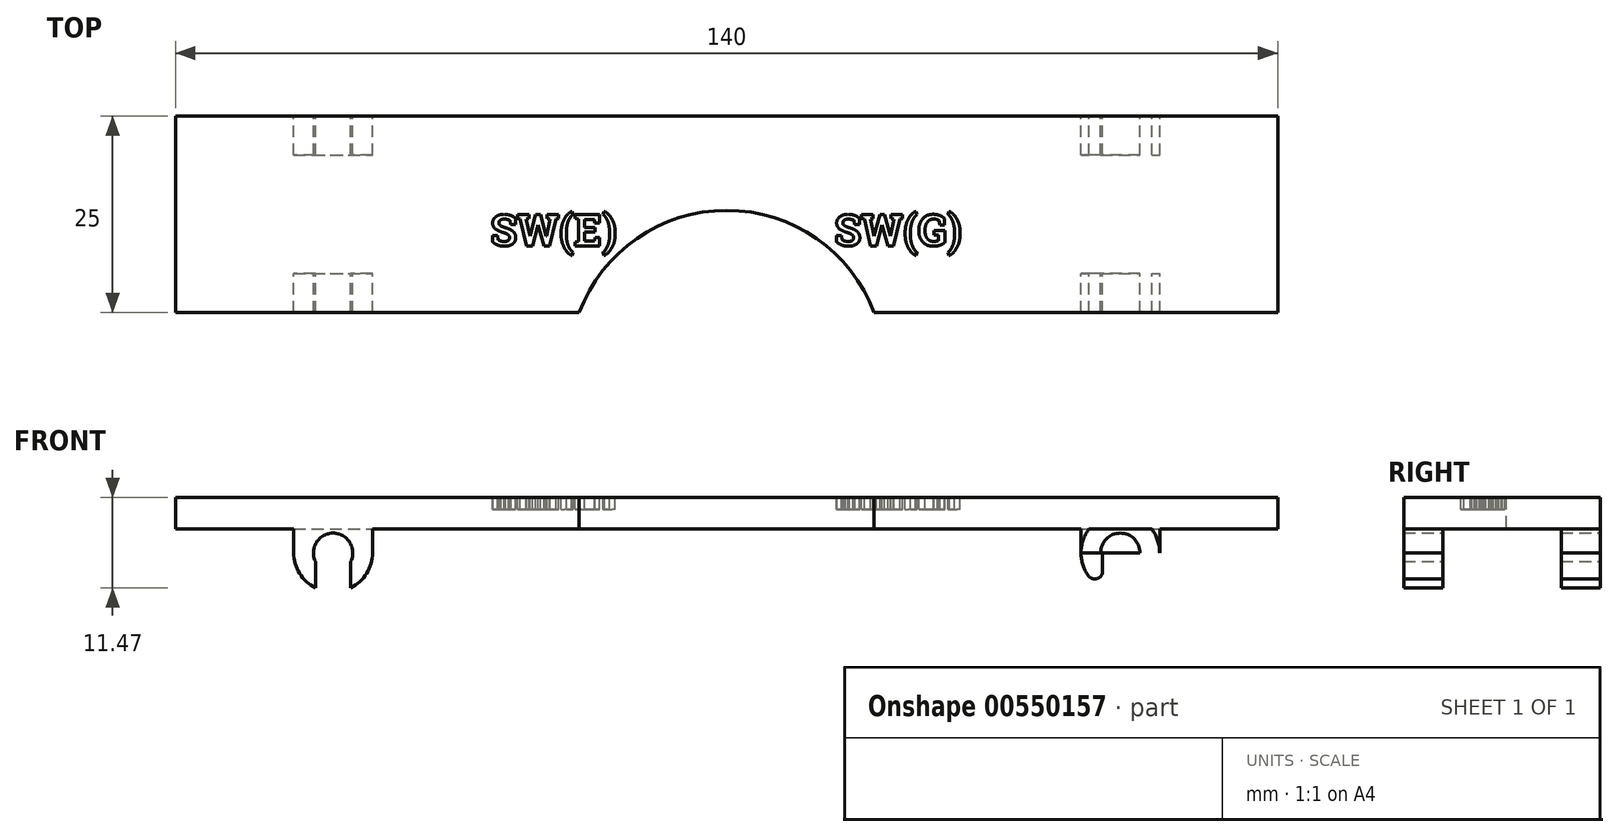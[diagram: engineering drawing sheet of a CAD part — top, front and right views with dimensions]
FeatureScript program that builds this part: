
annotation { "Feature Type Name" : "Feature", "Feature Type Description" : "" }
export const myFeature = defineFeature(function(context is Context, id is Id, definition is map)
    precondition{}
    {
        {
            var Q0;
            Q0=qCreatedBy(makeId("Top.planeOp"),FACE);
            var sketch = newSketch(context, id + "F0", { "sketchPlane" : qUnion([Q0])});
            skLineSegment(sketch, "E0.bottom", {"start": v(-70, 12.5) * mm, "end": v(70, 12.5) * mm});
            skLineSegment(sketch, "E0.top", {"start": v(-70, -12.5) * mm, "end": v(70, -12.5) * mm});
            skLineSegment(sketch, "E0.left", {"start": v(-70, 12.5) * mm, "end": v(-70, -12.5) * mm});
            skLineSegment(sketch, "E0.right", {"start": v(70, 12.5) * mm, "end": v(70, -12.5) * mm});
            skCircle(sketch, "E1", {"center": v(0, -19.5) * mm, "radius": 20 * mm});
            skSolve(sketch);
        }
        {
            var Q0;
            Q0=makeQuery(id+"F0.imprint","IMPRINT",FACE,{"disambiguationData":[TD([[makeQuery(id+"F0.imprint","IMPRINT",EDGE,{"derivedFrom":sQuery(id+"F0.wireOp",EDGE,"E0.bottom")}),-1.0]])]});
            var Q1;
            Q1=makeQuery(id+"F0.imprint","IMPRINT",FACE,{"disambiguationData":[TD([[makeQuery(id+"F0.imprint","IMPRINT",EDGE,{"derivedFrom":sQuery(id+"F0.wireOp",EDGE,"82b3bb51-51cf-4b73-bf01-d6abe3403867.sketch_text.stroke-86")}),1.0]])]});
            var Q2;
            Q2=makeQuery(id+"F0.imprint","IMPRINT",FACE,{"disambiguationData":[TD([[makeQuery(id+"F0.imprint","IMPRINT",EDGE,{"derivedFrom":sQuery(id+"F0.wireOp",EDGE,"82b3bb51-51cf-4b73-bf01-d6abe3403867.sketch_text.stroke-79")}),1.0]])]});
            var Q3;
            Q3=makeQuery(id+"F0.imprint","IMPRINT",FACE,{"disambiguationData":[TD([[makeQuery(id+"F0.imprint","IMPRINT",EDGE,{"derivedFrom":sQuery(id+"F0.wireOp",EDGE,"82b3bb51-51cf-4b73-bf01-d6abe3403867.sketch_text.stroke-171")}),1.0]])]});
            var Q4;
            Q4=makeQuery(id+"F0.imprint","IMPRINT",FACE,{"disambiguationData":[TD([[makeQuery(id+"F0.imprint","IMPRINT",EDGE,{"derivedFrom":sQuery(id+"F0.wireOp",EDGE,"82b3bb51-51cf-4b73-bf01-d6abe3403867.sketch_text.stroke-197")}),1.0]])]});
            var Q5;
            Q5=makeQuery(id+"F0.imprint","IMPRINT",FACE,{"disambiguationData":[TD([[makeQuery(id+"F0.imprint","IMPRINT",EDGE,{"derivedFrom":sQuery(id+"F0.wireOp",EDGE,"82b3bb51-51cf-4b73-bf01-d6abe3403867.sketch_text.stroke-220")}),1.0]])]});
            extrude(context, id + "F1", {"entities" : qUnion([Q0, Q1, Q2, Q3, Q4, Q5]), "depth" : 4 * mm, "offsetDistance" : 25 * mm});
        }
        {
            var Q0;
            Q0=makeQuery(id+"F1.opExtrude","CAP_FACE",FACE,{"disambiguationData":[OSD([sQuery(id+"F0.wireOp",EDGE,"E0.bottom"),sQuery(id+"F0.wireOp",EDGE,"E0.top"),sQuery(id+"F0.wireOp",EDGE,"E0.left"),sQuery(id+"F0.wireOp",EDGE,"E0.right"),sQuery(id+"F0.wireOp",EDGE,"E1")])],"isStart":false});
            var sketch = newSketch(context, id + "F2", { "sketchPlane" : qUnion([Q0])});
            skText(sketch, "E2", { "text": "SW(E)", "fontName": "RobotoSlab-Bold.ttf"});
            skText(sketch, "E3", { "text": "SW(G)", "fontName": "RobotoSlab-Bold.ttf"});
            const initialGuessF2  = {"E2": [-0.03, -0.004, 1, 0, 0.004], "E3": [0.0137, -0.004, 1, 0, 0.004]};
            skSetInitialGuess(sketch, initialGuessF2);
            skSolve(sketch);
        }
        {
            var Q0;
            Q0 = qSketchRegion(id + "F2", true);
            extrude(context, id + "F3", {"entities" : qUnion([Q0]), "operationType" : NewBodyOperationType.REMOVE, "oppositeDirection" : true, "depth" : 1.5 * mm, "offsetDistance" : 25 * mm});
        }
        {
            var Q0;
            Q0=makeQuery(id+"F1.opExtrude","SWEPT_FACE",FACE,{"disambiguationData":[OSD([sQuery(id+"F0.wireOp",EDGE,"E0.bottom")])]});
            var sketch = newSketch(context, id + "F4", { "sketchPlane" : qUnion([Q0])});
            skCircle(sketch, "E4", {"center": v(50, -3) * mm, "radius": 2.5 * mm});
            skCircle(sketch, "E5", {"center": v(50, -3) * mm, "radius": 5 * mm});
            skLineSegment(sketch, "E6.bottom", {"start": v(52.25, -11.19) * mm, "end": v(47.75, -11.19) * mm});
            skLineSegment(sketch, "E6.top", {"start": v(52.25, -3) * mm, "end": v(47.75, -3) * mm});
            skLineSegment(sketch, "E6.left", {"start": v(52.25, -11.19) * mm, "end": v(52.25, -3) * mm});
            skLineSegment(sketch, "E6.right", {"start": v(47.75, -11.19) * mm, "end": v(47.75, -3) * mm});
            skLineSegment(sketch, "E7.bottom", {"start": v(55, -3) * mm, "end": v(45, -3) * mm});
            skLineSegment(sketch, "E7.top", {"start": v(55, 0) * mm, "end": v(45, 0) * mm});
            skLineSegment(sketch, "E7.left", {"start": v(55, -3) * mm, "end": v(55, 0) * mm});
            skLineSegment(sketch, "E7.right", {"start": v(45, -3) * mm, "end": v(45, 0) * mm});
            skLineSegment(sketch, "E8.MirrorCS", {"start": v(-55, -3) * mm, "end": v(-45, -3) * mm});
            skLineSegment(sketch, "E9.MirrorCS", {"start": v(-55, -3) * mm, "end": v(-55, 0) * mm});
            skLineSegment(sketch, "E10.MirrorCS", {"start": v(-45, -3) * mm, "end": v(-45, 0) * mm});
            skLineSegment(sketch, "E11.MirrorCS", {"start": v(-52.25, -3) * mm, "end": v(-47.75, -3) * mm});
            skLineSegment(sketch, "E12.MirrorCS", {"start": v(-47.75, -11.19) * mm, "end": v(-47.75, -3) * mm});
            skCircle(sketch, "E13.MirrorC", {"center": v(-50, -3) * mm, "radius": 2.5 * mm});
            skCircle(sketch, "E14.MirrorC", {"center": v(-50, -3) * mm, "radius": 5 * mm});
            skLineSegment(sketch, "E15.MirrorCS", {"start": v(-52.25, -11.19) * mm, "end": v(-52.25, -3) * mm});
            skLineSegment(sketch, "E16.MirrorCS", {"start": v(-52.25, -11.19) * mm, "end": v(-47.75, -11.19) * mm});
            skSolve(sketch);
        }
        {
            var Q0;
            {var subQ0=sQuery(id+"F4.wireOp",EDGE,"E7.bottom");var subQ1=sQuery(id+"F4.wireOp",EDGE,"E4");var subQ2=makeQuery(id+"F4.imprint","INTERSECT",VERTEX,{"disambiguationData":[OD(1.0)],"derivedFrom":[subQ1,subQ0]});Q0=makeQuery(id+"F4.imprint","IMPRINT",FACE,{"disambiguationData":[TD([[makeQuery(id+"F4.imprint","IMPRINT",EDGE,{"disambiguationData":[TD([[subQ2,1.0]])],"derivedFrom":subQ1}),-1.0]])]});}
            var Q1;
            {var subQ0=sQuery(id+"F4.wireOp",EDGE,"E7.bottom");var subQ3=sQuery(id+"F4.wireOp",EDGE,"E4");var subQ9=makeQuery(id+"F4.imprint","INTERSECT",VERTEX,{"disambiguationData":[OD(0.0)],"derivedFrom":[subQ3,subQ0]});Q1=makeQuery(id+"F4.imprint","IMPRINT",FACE,{"disambiguationData":[TD([[makeQuery(id+"F4.imprint","IMPRINT",EDGE,{"disambiguationData":[TD([[subQ9,1.0]])],"derivedFrom":subQ3}),-1.0]])]});}
            var Q2;
            {var subQ0=sQuery(id+"F4.wireOp",EDGE,"E7.bottom");var subQ1=sQuery(id+"F4.wireOp",EDGE,"E4");var subQ2=makeQuery(id+"F4.imprint","INTERSECT",VERTEX,{"disambiguationData":[OD(0.0)],"derivedFrom":[subQ1,subQ0]});Q2=makeQuery(id+"F4.imprint","IMPRINT",FACE,{"disambiguationData":[TD([[makeQuery(id+"F4.imprint","IMPRINT",EDGE,{"disambiguationData":[TD([[subQ2,-1.0]])],"derivedFrom":subQ1}),-1.0]])]});}
            var Q3;
            {var subQ0=sQuery(id+"F4.wireOp",EDGE,"E7.right");Q3=makeQuery(id+"F4.imprint","IMPRINT",FACE,{"disambiguationData":[TD([[makeQuery(id+"F4.imprint","IMPRINT",EDGE,{"derivedFrom":subQ0}),-1.0]])]});}
            var Q4;
            {var subQ0=sQuery(id+"F4.wireOp",EDGE,"E7.left");Q4=makeQuery(id+"F4.imprint","IMPRINT",FACE,{"disambiguationData":[TD([[makeQuery(id+"F4.imprint","IMPRINT",EDGE,{"derivedFrom":subQ0}),1.0]])]});}
            var Q5;
            {var subQ1=sQuery(id+"F4.wireOp",EDGE,"E8.MirrorCS");var subQ3=sQuery(id+"F4.wireOp",EDGE,"E13.MirrorC");var subQ4=makeQuery(id+"F4.imprint","INTERSECT",VERTEX,{"disambiguationData":[OD(0.0)],"derivedFrom":[subQ1,subQ3]});Q5=makeQuery(id+"F4.imprint","IMPRINT",FACE,{"disambiguationData":[TD([[makeQuery(id+"F4.imprint","IMPRINT",EDGE,{"disambiguationData":[TD([[subQ4,1.0]])],"derivedFrom":subQ3}),1.0]])]});}
            var Q6;
            {var subQ1=sQuery(id+"F4.wireOp",EDGE,"E8.MirrorCS");var subQ6=sQuery(id+"F4.wireOp",EDGE,"E13.MirrorC");var subQ8=makeQuery(id+"F4.imprint","INTERSECT",VERTEX,{"disambiguationData":[OD(0.0)],"derivedFrom":[subQ1,subQ6]});Q6=makeQuery(id+"F4.imprint","IMPRINT",FACE,{"disambiguationData":[TD([[makeQuery(id+"F4.imprint","IMPRINT",EDGE,{"disambiguationData":[TD([[subQ8,-1.0]])],"derivedFrom":subQ6}),1.0]])]});}
            var Q7;
            {var subQ0=sQuery(id+"F4.wireOp",EDGE,"E14.MirrorC");var subQ5=sQuery(id+"F4.wireOp",EDGE,"E12.MirrorCS");var subQ6=makeQuery(id+"F4.imprint","INTERSECT",VERTEX,{"derivedFrom":[subQ5,subQ0]});Q7=makeQuery(id+"F4.imprint","IMPRINT",FACE,{"disambiguationData":[TD([[makeQuery(id+"F4.imprint","IMPRINT",EDGE,{"disambiguationData":[TD([[subQ6,-1.0]])],"derivedFrom":subQ5}),-1.0]])]});}
            var Q8;
            {var subQ0=sQuery(id+"F4.wireOp",EDGE,"E10.MirrorCS");Q8=makeQuery(id+"F4.imprint","IMPRINT",FACE,{"disambiguationData":[TD([[makeQuery(id+"F4.imprint","IMPRINT",EDGE,{"derivedFrom":subQ0}),1.0]])]});}
            var Q9;
            {var subQ0=sQuery(id+"F4.wireOp",EDGE,"E9.MirrorCS");Q9=makeQuery(id+"F4.imprint","IMPRINT",FACE,{"disambiguationData":[TD([[makeQuery(id+"F4.imprint","IMPRINT",EDGE,{"derivedFrom":subQ0}),-1.0]])]});}
            extrude(context, id + "F5", {"entities" : qUnion([Q0, Q1, Q2, Q3, Q4, Q5, Q6, Q7, Q8, Q9]), "operationType" : NewBodyOperationType.ADD, "oppositeDirection" : true, "depth" : 5 * mm, "offsetDistance" : 25 * mm});
        }
        {
            var Q0;
            {var subQ1=sQuery(id+"F4.wireOp",EDGE,"E8.MirrorCS");var subQ6=sQuery(id+"F4.wireOp",EDGE,"E13.MirrorC");var subQ8=makeQuery(id+"F4.imprint","INTERSECT",VERTEX,{"disambiguationData":[OD(0.0)],"derivedFrom":[subQ1,subQ6]});Q0=makeQuery(id+"F4.imprint","IMPRINT",FACE,{"disambiguationData":[TD([[makeQuery(id+"F4.imprint","IMPRINT",EDGE,{"disambiguationData":[TD([[subQ8,-1.0]])],"derivedFrom":subQ6}),1.0]])]});}
            var Q1;
            {var subQ1=sQuery(id+"F4.wireOp",EDGE,"E8.MirrorCS");var subQ3=sQuery(id+"F4.wireOp",EDGE,"E13.MirrorC");var subQ4=makeQuery(id+"F4.imprint","INTERSECT",VERTEX,{"disambiguationData":[OD(0.0)],"derivedFrom":[subQ1,subQ3]});Q1=makeQuery(id+"F4.imprint","IMPRINT",FACE,{"disambiguationData":[TD([[makeQuery(id+"F4.imprint","IMPRINT",EDGE,{"disambiguationData":[TD([[subQ4,1.0]])],"derivedFrom":subQ3}),1.0]])]});}
            var Q2;
            {var subQ0=sQuery(id+"F4.wireOp",EDGE,"E14.MirrorC");var subQ5=sQuery(id+"F4.wireOp",EDGE,"E12.MirrorCS");var subQ6=makeQuery(id+"F4.imprint","INTERSECT",VERTEX,{"derivedFrom":[subQ5,subQ0]});Q2=makeQuery(id+"F4.imprint","IMPRINT",FACE,{"disambiguationData":[TD([[makeQuery(id+"F4.imprint","IMPRINT",EDGE,{"disambiguationData":[TD([[subQ6,-1.0]])],"derivedFrom":subQ5}),-1.0]])]});}
            var Q3;
            {var subQ0=sQuery(id+"F4.wireOp",EDGE,"E10.MirrorCS");Q3=makeQuery(id+"F4.imprint","IMPRINT",FACE,{"disambiguationData":[TD([[makeQuery(id+"F4.imprint","IMPRINT",EDGE,{"derivedFrom":subQ0}),1.0]])]});}
            var Q4;
            {var subQ0=sQuery(id+"F4.wireOp",EDGE,"E9.MirrorCS");Q4=makeQuery(id+"F4.imprint","IMPRINT",FACE,{"disambiguationData":[TD([[makeQuery(id+"F4.imprint","IMPRINT",EDGE,{"derivedFrom":subQ0}),-1.0]])]});}
            var Q5;
            {var subQ0=sQuery(id+"F4.wireOp",EDGE,"E7.bottom");var subQ1=sQuery(id+"F4.wireOp",EDGE,"E4");var subQ2=makeQuery(id+"F4.imprint","INTERSECT",VERTEX,{"disambiguationData":[OD(0.0)],"derivedFrom":[subQ1,subQ0]});Q5=makeQuery(id+"F4.imprint","IMPRINT",FACE,{"disambiguationData":[TD([[makeQuery(id+"F4.imprint","IMPRINT",EDGE,{"disambiguationData":[TD([[subQ2,-1.0]])],"derivedFrom":subQ1}),-1.0]])]});}
            var Q6;
            {var subQ0=sQuery(id+"F4.wireOp",EDGE,"E7.bottom");var subQ3=sQuery(id+"F4.wireOp",EDGE,"E4");var subQ9=makeQuery(id+"F4.imprint","INTERSECT",VERTEX,{"disambiguationData":[OD(0.0)],"derivedFrom":[subQ3,subQ0]});Q6=makeQuery(id+"F4.imprint","IMPRINT",FACE,{"disambiguationData":[TD([[makeQuery(id+"F4.imprint","IMPRINT",EDGE,{"disambiguationData":[TD([[subQ9,1.0]])],"derivedFrom":subQ3}),-1.0]])]});}
            var Q7;
            {var subQ0=sQuery(id+"F4.wireOp",EDGE,"E7.bottom");var subQ1=sQuery(id+"F4.wireOp",EDGE,"E4");var subQ2=makeQuery(id+"F4.imprint","INTERSECT",VERTEX,{"disambiguationData":[OD(1.0)],"derivedFrom":[subQ1,subQ0]});Q7=makeQuery(id+"F4.imprint","IMPRINT",FACE,{"disambiguationData":[TD([[makeQuery(id+"F4.imprint","IMPRINT",EDGE,{"disambiguationData":[TD([[subQ2,1.0]])],"derivedFrom":subQ1}),-1.0]])]});}
            var Q8;
            {var subQ0=sQuery(id+"F4.wireOp",EDGE,"E7.left");Q8=makeQuery(id+"F4.imprint","IMPRINT",FACE,{"disambiguationData":[TD([[makeQuery(id+"F4.imprint","IMPRINT",EDGE,{"derivedFrom":subQ0}),1.0]])]});}
            var Q9;
            {var subQ0=sQuery(id+"F4.wireOp",EDGE,"E7.right");Q9=makeQuery(id+"F4.imprint","IMPRINT",FACE,{"disambiguationData":[TD([[makeQuery(id+"F4.imprint","IMPRINT",EDGE,{"derivedFrom":subQ0}),-1.0]])]});}
            extrude(context, id + "F6", {"entities" : qUnion([Q0, Q1, Q2, Q3, Q4, Q5, Q6, Q7, Q8, Q9]), "operationType" : NewBodyOperationType.ADD, "oppositeDirection" : true, "depth" : 25 * mm, "offsetDistance" : 25 * mm, "hasSecondDirection" : true, "secondDirectionOppositeDirection" : true, "secondDirectionDepth" : 20 * mm});
        }
        {
            var Q0;
            Q0=makeQuery(id+"F5.opExtrude","SWEPT_EDGE",EDGE,{"disambiguationData":[OSD([sQuery(id+"F4.wireOp",EDGE,"E5"),sQuery(id+"F4.wireOp",EDGE,"E6.right")])]});
            var Q1;
            Q1=makeQuery(id+"F6.opExtrude","SWEPT_EDGE",EDGE,{"disambiguationData":[OSD([sQuery(id+"F4.wireOp",EDGE,"E5"),sQuery(id+"F4.wireOp",EDGE,"E6.right")])]});
            var Q2;
            Q2=makeQuery(id+"F5.opExtrude","SWEPT_EDGE",EDGE,{"disambiguationData":[OSD([sQuery(id+"F4.wireOp",EDGE,"E5"),sQuery(id+"F4.wireOp",EDGE,"E6.left")])]});
            var Q3;
            Q3=makeQuery(id+"F6.opExtrude","SWEPT_EDGE",EDGE,{"disambiguationData":[OSD([sQuery(id+"F4.wireOp",EDGE,"E5"),sQuery(id+"F4.wireOp",EDGE,"E6.left")])]});
            var Q4;
            Q4=makeQuery(id+"F5.opExtrude","SWEPT_EDGE",EDGE,{"disambiguationData":[OSD([sQuery(id+"F4.wireOp",EDGE,"E12.MirrorCS"),sQuery(id+"F4.wireOp",EDGE,"E14.MirrorC")])]});
            var Q5;
            Q5=makeQuery(id+"F6.opExtrude","SWEPT_EDGE",EDGE,{"disambiguationData":[OSD([sQuery(id+"F4.wireOp",EDGE,"E12.MirrorCS"),sQuery(id+"F4.wireOp",EDGE,"E14.MirrorC")])]});
            var Q6;
            Q6=makeQuery(id+"F6.opExtrude","SWEPT_EDGE",EDGE,{"disambiguationData":[OSD([sQuery(id+"F4.wireOp",EDGE,"E14.MirrorC"),sQuery(id+"F4.wireOp",EDGE,"E15.MirrorCS")])]});
            var Q7;
            Q7=makeQuery(id+"F5.opExtrude","SWEPT_EDGE",EDGE,{"disambiguationData":[OSD([sQuery(id+"F4.wireOp",EDGE,"E14.MirrorC"),sQuery(id+"F4.wireOp",EDGE,"E15.MirrorCS")])]});
            var Q8;
            Q8=makeQuery(id+"F1.opExtrude","CAP_EDGE",EDGE,{"disambiguationData":[OSD([sQuery(id+"F0.wireOp",EDGE,"E1")])],"isStart":true});
            var Q9;
            Q9=makeQuery(id+"F1.opExtrude","CAP_FACE",FACE,{"disambiguationData":[OSD([sQuery(id+"F0.wireOp",EDGE,"E0.bottom"),sQuery(id+"F0.wireOp",EDGE,"E0.top"),sQuery(id+"F0.wireOp",EDGE,"E0.left"),sQuery(id+"F0.wireOp",EDGE,"E0.right"),sQuery(id+"F0.wireOp",EDGE,"E1")])],"isStart":true});
            var Q10;
            Q10=makeQuery(id+"F1.opExtrude","SWEPT_EDGE",EDGE,{"disambiguationData":[OSD([sQuery(id+"F0.wireOp",EDGE,"E0.bottom"),sQuery(id+"F0.wireOp",EDGE,"E0.left")])]});
            var Q11;
            Q11=makeQuery(id+"F1.opExtrude","SWEPT_EDGE",EDGE,{"disambiguationData":[OSD([sQuery(id+"F0.wireOp",EDGE,"E0.top"),sQuery(id+"F0.wireOp",EDGE,"E0.left")])]});
            var Q12;
            {var subQ0=sQuery(id+"F0.wireOp",EDGE,"E1");var subQ1=sQuery(id+"F0.wireOp",EDGE,"E0.top");Q12=makeQuery(id+"F1.opExtrude","SWEPT_EDGE",EDGE,{"disambiguationData":[OSD([subQ1,subQ0]),TDD([makeQuery(id+"F0.imprint","INTERSECT",VERTEX,{"disambiguationData":[OD(0.0)],"derivedFrom":[subQ1,subQ0]})])]});}
            var Q13;
            {var subQ0=sQuery(id+"F0.wireOp",EDGE,"E1");var subQ1=sQuery(id+"F0.wireOp",EDGE,"E0.top");Q13=makeQuery(id+"F1.opExtrude","SWEPT_EDGE",EDGE,{"disambiguationData":[OSD([subQ1,subQ0]),TDD([makeQuery(id+"F0.imprint","INTERSECT",VERTEX,{"disambiguationData":[OD(1.0)],"derivedFrom":[subQ1,subQ0]})])]});}
            var Q14;
            Q14=makeQuery(id+"F1.opExtrude","SWEPT_EDGE",EDGE,{"disambiguationData":[OSD([sQuery(id+"F0.wireOp",EDGE,"E0.top"),sQuery(id+"F0.wireOp",EDGE,"E0.right")])]});
            var Q15;
            Q15=makeQuery(id+"F1.opExtrude","SWEPT_EDGE",EDGE,{"disambiguationData":[OSD([sQuery(id+"F0.wireOp",EDGE,"E0.bottom"),sQuery(id+"F0.wireOp",EDGE,"E0.right")])]});
            fillet(context, id + "F7", {"entities" : qUnion([Q0, Q1, Q2, Q3, Q4, Q5, Q6, Q7, Q8, Q9, Q10, Q11, Q12, Q13, Q14, Q15]), "radius" : 1 * mm, "tangentPropagation" : true, "allowEdgeOverflow" : false});
        }
    });
